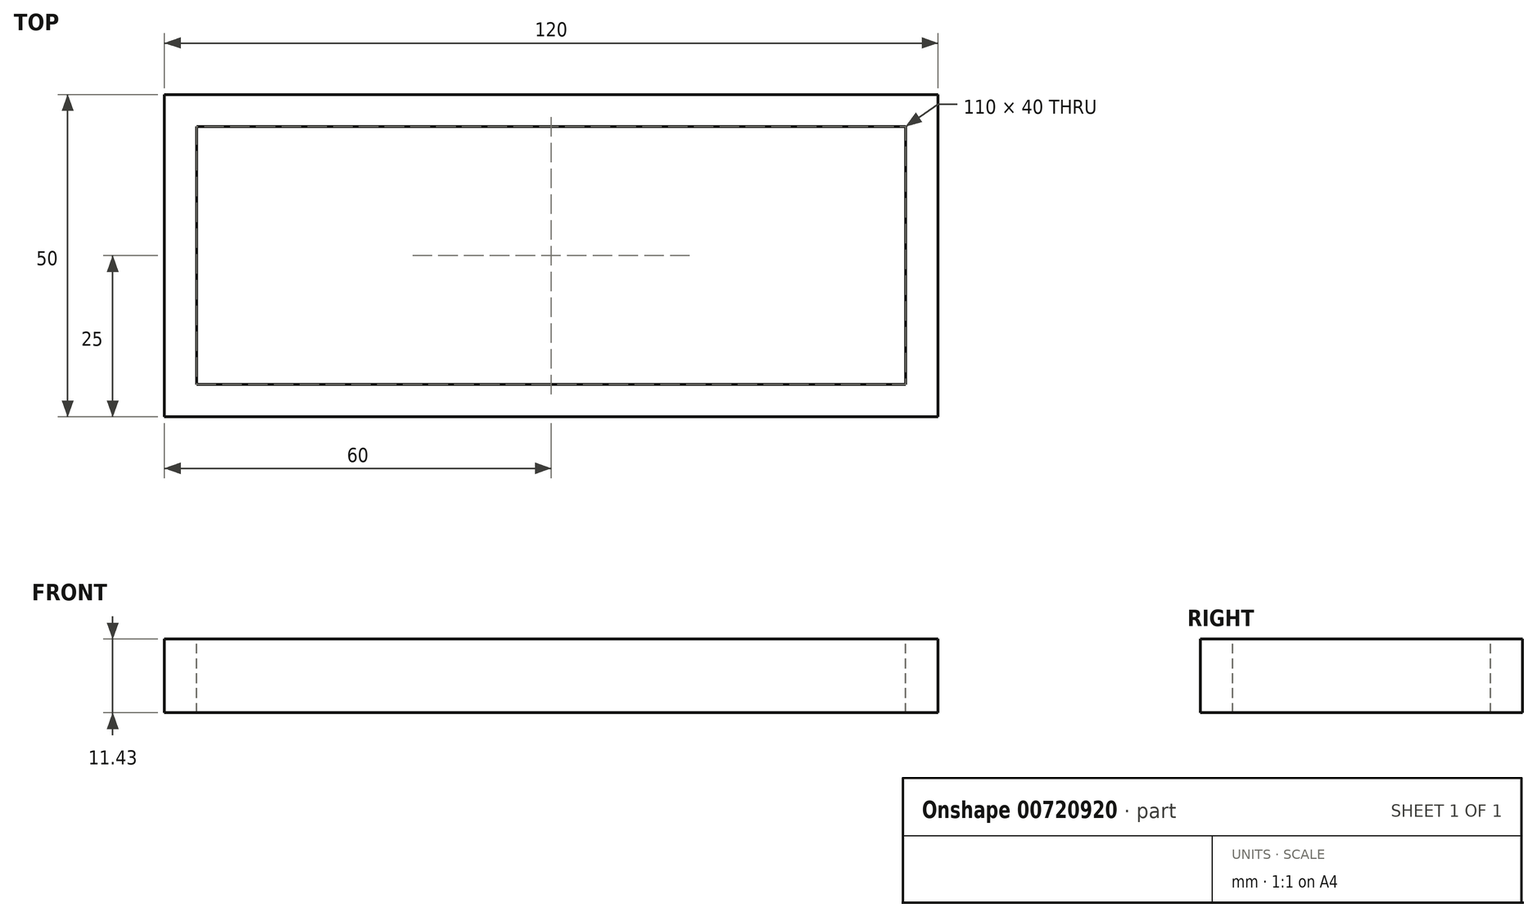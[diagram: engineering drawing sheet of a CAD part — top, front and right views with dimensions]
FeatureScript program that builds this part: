
annotation { "Feature Type Name" : "Feature", "Feature Type Description" : "" }
export const myFeature = defineFeature(function(context is Context, id is Id, definition is map)
    precondition{}
    {
        {
            var Q0;
            Q0=qCreatedBy(makeId("Top.planeOp"),FACE);
            var sketch = newSketch(context, id + "F0", { "sketchPlane" : qUnion([Q0])});
            skLineSegment(sketch, "E0.bottom", {"start": v(55, 20) * mm, "end": v(-55, 20) * mm});
            skLineSegment(sketch, "E0.top", {"start": v(55, -20) * mm, "end": v(-55, -20) * mm});
            skLineSegment(sketch, "E0.left", {"start": v(55, 20) * mm, "end": v(55, -20) * mm});
            skLineSegment(sketch, "E0.right", {"start": v(-55, 20) * mm, "end": v(-55, -20) * mm});
            skPoint(sketch, "E0.middle", {"position": v(0, 0) * mm});
            skLineSegment(sketch, "E1.bottom", {"start": v(60, 25) * mm, "end": v(-60, 25) * mm});
            skLineSegment(sketch, "E1.top", {"start": v(60, -25) * mm, "end": v(-60, -25) * mm});
            skLineSegment(sketch, "E1.left", {"start": v(60, 25) * mm, "end": v(60, -25) * mm});
            skLineSegment(sketch, "E1.right", {"start": v(-60, 25) * mm, "end": v(-60, -25) * mm});
            skSolve(sketch);
        }
        {
            var Q0;
            Q0=makeQuery(id+"F0.imprint","IMPRINT",FACE,{"disambiguationData":[TD([[makeQuery(id+"F0.imprint","IMPRINT",EDGE,{"derivedFrom":sQuery(id+"F0.wireOp",EDGE,"E0.bottom")}),-1.0]])]});
            extrude(context, id + "F1", {"entities" : qUnion([Q0]), "oppositeDirection" : true, "depth" : 11.43 * mm, "offsetDistance" : 25.4 * mm});
        }
    });
